# Revit family: QF_BRITA_VIV Fill 200 CT_ENG
name_source: partatom
category: Specialty Equipment
revit_build: Autodesk Revit 2018 (Build: 20170223_1515(x64)
units: mm (PartAtom-declared; Revit-internal decimal feet)

## family parameters
Always vertical = Yes
Cut with Voids When Loaded = No
OmniClass Number = 23.40.40.00
OmniClass Title = Food Service Equipment and Furnishings
Part Type = Normal
Room Calculation Point = No
Round Connector Dimension = Use Diameter
Shared = No
Work Plane-Based = No

## types (1)
- VIV Fill 200 CT
    Cold Water Flow = 2.0 L/s
    Cold Water Maximum Pressure = 400000.0 Pa
    Cold Water Minimum Pressure = 250000.0 Pa
    Cold Water Size = 0 mm
    Depth Actual = 595 mm  [stored 1.9521 ft]
    Description = VIV F 200 CT
    Direct Waste Size = 0 mm
    Electric power = 0 W
    Foodservice Equipment Identifier = Yes
    Height Actual = 545 mm  [stored 1.78806 ft]
    Length Actual = 400 mm  [stored 1.31234 ft]
    Manufacturer = BRITA GmbH
    Max Overcurrent Protection = 0 A
    Model = VIV F 200 CT
    Number of Poles = 1
    URL = http://www.brita.net
    URL Cutsheet = http://www.brita.net
    URL Manufacturer = http://www.brita.net
    URL Recommended Spares List = http://www.brita.net
    Volts = 0 V
    Weight = 42.00 kg

note: [stored X ft] marks values corroborated as IEEE doubles in the binary element streams (Revit-internal decimal feet)
